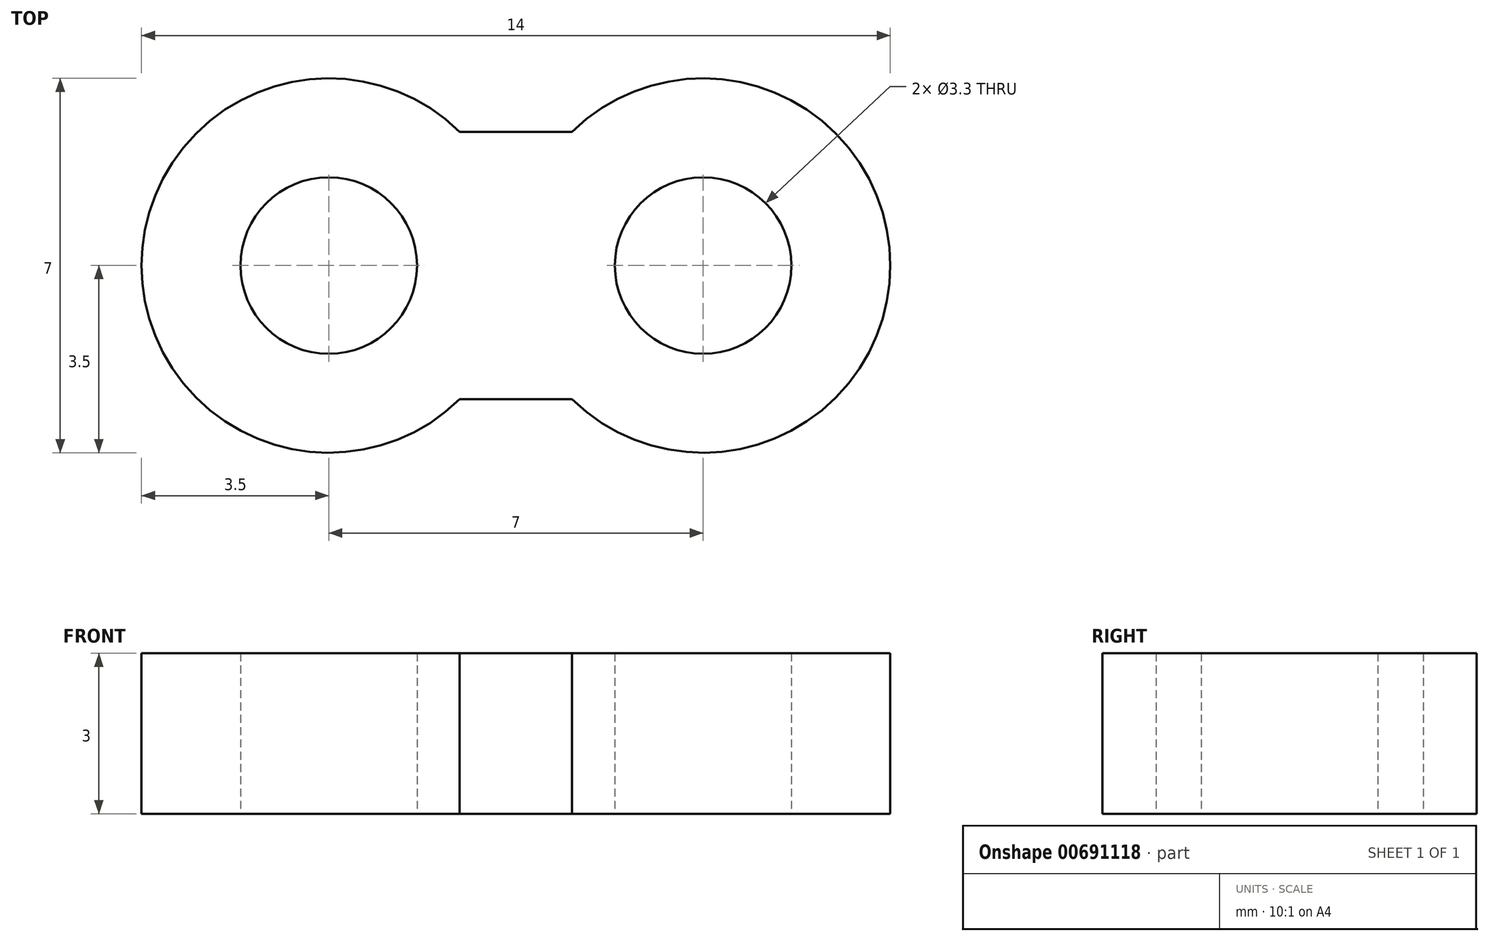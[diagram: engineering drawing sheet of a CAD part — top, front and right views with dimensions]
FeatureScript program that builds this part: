
annotation { "Feature Type Name" : "Feature", "Feature Type Description" : "" }
export const myFeature = defineFeature(function(context is Context, id is Id, definition is map)
    precondition{}
    {
        {
            var Q0;
            Q0=qCreatedBy(makeId("Top.planeOp"),FACE);
            var sketch = newSketch(context, id + "F0", { "sketchPlane" : qUnion([Q0])});
            skLineSegment(sketch, "E0", {"start": v(-3.5, 0) * mm, "end": v(3.5, 0) * mm, "construction": true});
            skArc(sketch, "E1", {"start": v(-1.05, 2.5) * mm, "mid": v(-7, 0) * mm, "end": v(-1.05, -2.5) * mm});
            skArc(sketch, "E2", {"start": v(1.05, -2.5) * mm, "mid": v(7, 0) * mm, "end": v(1.05, 2.5) * mm});
            skLineSegment(sketch, "E3", {"start": v(-1.05, 2.5) * mm, "end": v(1.05, 2.5) * mm});
            skLineSegment(sketch, "E4.MirrorCS", {"start": v(-1.05, -2.5) * mm, "end": v(1.05, -2.5) * mm});
            skCircle(sketch, "E5", {"center": v(-3.5, 0) * mm, "radius": 1.65 * mm});
            skCircle(sketch, "E6", {"center": v(3.5, 0) * mm, "radius": 1.65 * mm});
            skSolve(sketch);
        }
        {
            var Q0;
            Q0=makeQuery(id+"F0.imprint","IMPRINT",FACE,{"disambiguationData":[TD([[makeQuery(id+"F0.imprint","IMPRINT",EDGE,{"derivedFrom":sQuery(id+"F0.wireOp",EDGE,"E1")}),1.0]])]});
            extrude(context, id + "F1", {"entities" : qUnion([Q0]), "depth" : 3 * mm, "offsetDistance" : 25 * mm});
        }
    });
